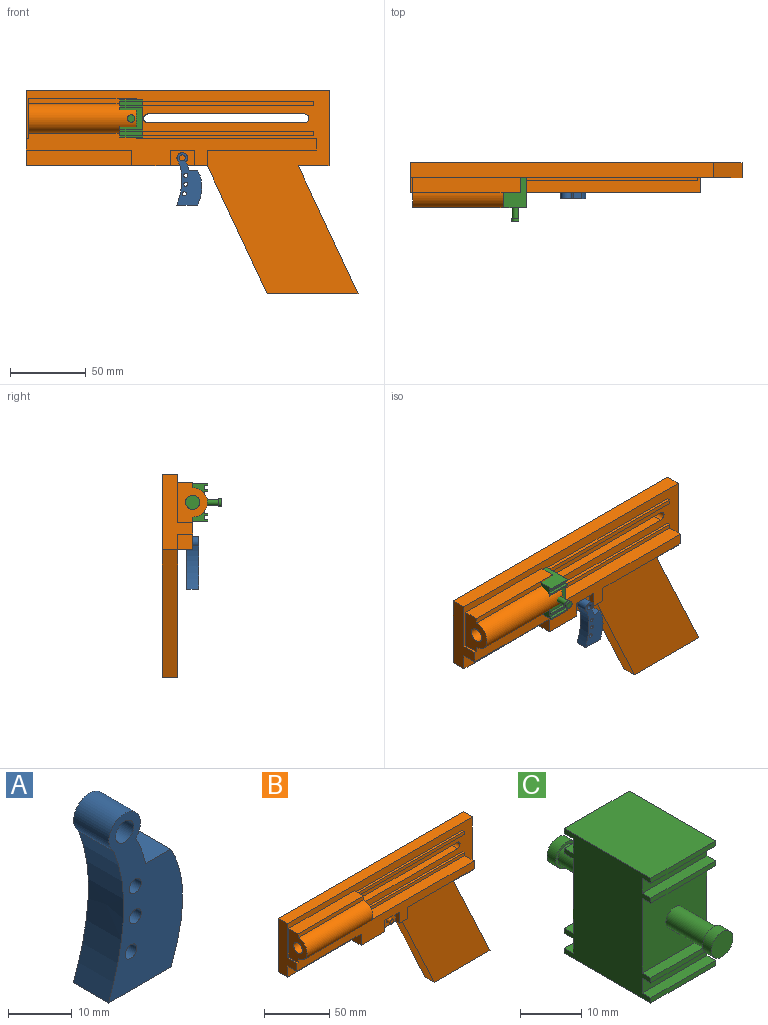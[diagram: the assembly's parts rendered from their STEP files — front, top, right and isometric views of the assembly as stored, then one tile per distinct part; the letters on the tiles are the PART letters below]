
ASSEMBLY  parts=3 mates=2
PART A: 13 faces, bbox 17.5x7.8x34.6 mm
  f0: plane 7.8x5.59mm, normal (0,0,1), area 43.6mm2, adj f1,f9,f11,f12
  f1: extruded ~7.8x5.93mm, area 49.6mm2, adj f0,f2,f11,f12
  f2: cylinder r=3.5mm len=7.8mm, axis (0,1,0), area 129.7mm2, adj f1,f3,f11,f12
  f3: extruded ~28.54x7.8mm, area 228.1mm2, adj f2,f4,f11,f12
  f4: plane 7.8x5.31mm, normal (-0.01,0,-1), area 41.4mm2, adj f3,f5,f11,f12
  f5: plane 8.48x7.8mm, normal (0,0,-1), area 66.1mm2, adj f4,f9,f11,f12
  f6: cylinder r=1.31mm len=7.8mm, axis (0,1,0), area 64.1mm2, adj f11,f12
  f7: cylinder r=1.31mm len=7.8mm, axis (0,1,0), area 64.1mm2, adj f11,f12
  f8: cylinder r=2mm len=7.8mm, axis (0,1,0), area 98mm2, adj f11,f12
  f9: extruded ~22.64x7.8mm, area 182.9mm2, adj f0,f5,f11,f12
  f10: cylinder r=1.31mm len=7.8mm, axis (0,1,0), area 64.1mm2, adj f11,f12
  f11: plane 34.6x17.46mm, normal (0,-1,0), area 333.6mm2, adj f0,f1,f2,f3,f4,f5,f6,f7
  f12: plane 34.6x17.46mm, normal (0,1,0), area 333.6mm2, adj f0,f1,f2,f3,f4,f5,f6,f7
PART B: 43 faces, bbox 219.1x29.7x134.5 mm
  f0: plane 119.24x10mm, normal (0,0,1), area 1192.4mm2, adj f3,f25,f28,f42
  f1: plane 69.74x10.47mm, normal (0,-1,0), area 730.2mm2, adj f8,f9,f27,f30
  f2: plane 72.17x10mm, normal (0,0,-1), area 721.7mm2, adj f3,f25,f28,f29
  f3: plane 219.13x134.46mm, normal (0,-1,0), area 9146.9mm2, adj f0,f2,f4,f5,f6,f7,f8,f10
  f4: plane 84.46x39.39mm, normal (0.91,0,0.42), area 931.9mm2, adj f3,f5,f11,f12
  f5: plane 20.26x10mm, normal (0,0,-1), area 202.6mm2, adj f3,f4,f6,f12
  f6: plane 50x10mm, normal (1,0,0), area 500mm2, adj f3,f5,f7,f12
  f7: plane 200x10mm, normal (0,0,1), area 2000mm2, adj f3,f6,f8,f12
  f8: plane 50x20mm, normal (-1,0,0), area 575.2mm2, adj f1,f3,f7,f9,f12,f26,f27,f28
  f9: plane 119.74x20mm, normal (0,0,-1), area 1633.9mm2, adj f1,f8,f10,f12,f28,f29,f30,f31
  f10: plane 84.46x39.39mm, normal (-0.91,0,-0.42), area 931.9mm2, adj f3,f9,f11,f12
  f11: plane 60x10mm, normal (0,0,-1), area 600mm2, adj f3,f4,f10,f12
  f12: plane 219.13x134.46mm, normal (0,1,0), area 14421.2mm2, adj f4,f5,f6,f7,f8,f9,f10,f11
  f13: plane 117.04x2mm, normal (0,0,-1), area 234.1mm2, adj f3,f14,f16,f42
  f14: plane 2.9x2mm, normal (1,0,0), area 5.8mm2, adj f3,f13,f15,f16
  f15: plane 117.04x2mm, normal (0,0,1), area 234.1mm2, adj f3,f14,f16,f42
  f16: plane 117.04x2.9mm, normal (0,-1,0), area 339.4mm2, adj f13,f14,f15,f42
  f17: plane 2.9x2mm, normal (1,0,0), area 5.8mm2, adj f3,f18,f19,f20
  f18: plane 117.04x2mm, normal (0,0,1), area 234.1mm2, adj f3,f17,f20,f42
  f19: plane 117.04x2mm, normal (0,0,-1), area 234.1mm2, adj f3,f17,f20,f42
  f20: plane 117.04x2.9mm, normal (0,-1,0), area 339.4mm2, adj f17,f18,f19,f42
  f21: cylinder r=3mm len=10mm, axis (0,1,0), area 94.2mm2, adj f3,f12,f22,f24
  f22: plane 103.05x10mm, normal (0,0,1), area 1030.5mm2, adj f3,f12,f21,f23
  f23: cylinder r=3mm len=10mm, axis (0,1,0), area 94.2mm2, adj f3,f12,f22,f24
  f24: plane 103.05x10mm, normal (0,0,-1), area 1030.5mm2, adj f3,f12,f21,f23
  f25: plane 10x7.52mm, normal (1,0,0), area 75.2mm2, adj f0,f2,f3,f28
  f26: plane 10x1.67mm, normal (0,0,1), area 16.7mm2, adj f3,f8,f28,f41
  f27: plane 69.74x10mm, normal (0,0,-1), area 697.4mm2, adj f1,f8,f28,f30
  f28: plane 191.91x21.64mm, normal (0,-1,0), area 2059.3mm2, adj f0,f2,f8,f9,f25,f26,f27,f29
  f29: plane 10.47x10mm, normal (1,0,0), area 104.7mm2, adj f2,f3,f9,f28
  f30: plane 10.47x10mm, normal (-1,0,0), area 104.7mm2, adj f1,f9,f27,f28
  f31: plane 10.47x4mm, normal (-1,0,0), area 41.9mm2, adj f9,f28,f32,f35
  f32: plane 15.88x4mm, normal (0,0,-1), area 63.5mm2, adj f28,f31,f34,f35
  f33: cylinder r=2mm len=4mm, axis (0,-1,0), area 50.3mm2, adj f35,f36
  f34: plane 10.47x4mm, normal (1,0,0), area 41.9mm2, adj f9,f28,f32,f35
  f35: plane 15.88x10.47mm, normal (0,-1,0), area 153.7mm2, adj f9,f31,f32,f33,f34
  f36: plane 4x4mm, normal (0,-1,0), area 12.6mm2, adj f33
  f37: cylinder r=9.72mm len=71mm, axis (1,0,0), area 2168.4mm2, adj f28,f38,f41,f42
  f38: plane 71x3.65mm, normal (0,-1,0), area 259.4mm2, adj f37,f39,f41,f42
  f39: plane 71x10mm, normal (0,0,1), area 710mm2, adj f3,f38,f41,f42
  f40: cylinder r=4.75mm len=71mm, axis (1,0,0), area 2119mm2, adj f41,f42
  f41: plane 26.75x19.72mm, normal (-1,0,0), area 345.1mm2, adj f3,f26,f28,f37,f38,f39,f40
  f42: plane 26.75x19.72mm, normal (1,0,0), area 333.5mm2, adj f0,f3,f13,f15,f16,f18,f19,f20
PART C: 38 faces, bbox 15x38x25 mm
  f0: plane 15x3mm, normal (0,1,0), area 45mm2, adj f7,f9,f34,f36
  f1: plane 15x15mm, normal (0,1,0), area 212.4mm2, adj f7,f9,f14,f31,f33
  f2: plane 15x3mm, normal (0,1,0), area 45mm2, adj f7,f9,f28,f30
  f3: plane 15x3mm, normal (0,-1,0), area 45mm2, adj f7,f9,f24,f26
  f4: plane 15x15mm, normal (0,-1,0), area 212.4mm2, adj f7,f9,f10,f21,f23
  f5: plane 15x3mm, normal (0,-1,0), area 45mm2, adj f7,f9,f18,f20
  f6: plane 20x15mm, normal (0,0,1), area 300mm2, adj f7,f9,f19,f29
  f7: plane 25x20mm, normal (-1,0,0), area 416mm2, adj f0,f1,f2,f3,f4,f5,f6,f8
  f8: plane 20x15mm, normal (0,0,-1), area 300mm2, adj f7,f9,f27,f37
  f9: plane 25x20mm, normal (1,0,0), area 416mm2, adj f0,f1,f2,f3,f4,f5,f6,f8
  f10: cylinder r=2mm len=9mm, axis (0,1,0), area 113.1mm2, adj f4,f13
  f11: cylinder r=2.5mm len=5mm, axis (0,1,0), area 31.4mm2, adj f12,f13
  f12: plane 5x5mm, normal (0,-1,0), area 19.6mm2, adj f11
  f13: plane 5x5mm, normal (0,1,0), area 7.1mm2, adj f10,f11
  f14: cylinder r=2mm len=9mm, axis (0,-1,0), area 113.1mm2, adj f1,f17
  f15: cylinder r=2.5mm len=5mm, axis (0,-1,0), area 31.4mm2, adj f16,f17
  f16: plane 5x5mm, normal (0,1,0), area 19.6mm2, adj f15
  f17: plane 5x5mm, normal (0,-1,0), area 7.1mm2, adj f14,f15
  f18: plane 15x2mm, normal (0,0,-1), area 30mm2, adj f5,f7,f9,f19
  f19: plane 15x1mm, normal (0,-1,0), area 15mm2, adj f6,f7,f9,f18
  f20: plane 15x2mm, normal (0,0,1), area 30mm2, adj f5,f7,f9,f22
  f21: plane 15x2mm, normal (0,0,-1), area 30mm2, adj f4,f7,f9,f22
  f22: plane 15x1mm, normal (0,-1,0), area 15mm2, adj f7,f9,f20,f21
  f23: plane 15x2mm, normal (0,0,1), area 30mm2, adj f4,f7,f9,f25
  f24: plane 15x2mm, normal (0,0,-1), area 30mm2, adj f3,f7,f9,f25
  f25: plane 15x1mm, normal (0,-1,0), area 15mm2, adj f7,f9,f23,f24
  f26: plane 15x2mm, normal (0,0,1), area 30mm2, adj f3,f7,f9,f27
  f27: plane 15x1mm, normal (0,-1,0), area 15mm2, adj f7,f8,f9,f26
  f28: plane 15x2mm, normal (0,0,-1), area 30mm2, adj f2,f7,f9,f29
  f29: plane 15x1mm, normal (0,1,0), area 15mm2, adj f6,f7,f9,f28
  f30: plane 15x2mm, normal (0,0,1), area 30mm2, adj f2,f7,f9,f32
  f31: plane 15x2mm, normal (0,0,-1), area 30mm2, adj f1,f7,f9,f32
  f32: plane 15x1mm, normal (0,1,0), area 15mm2, adj f7,f9,f30,f31
  f33: plane 15x2mm, normal (0,0,1), area 30mm2, adj f1,f7,f9,f35
  f34: plane 15x2mm, normal (0,0,-1), area 30mm2, adj f0,f7,f9,f35
  f35: plane 15x1mm, normal (0,1,0), area 15mm2, adj f7,f9,f33,f34
  f36: plane 15x2mm, normal (0,0,1), area 30mm2, adj f0,f7,f9,f37
  f37: plane 15x1mm, normal (0,1,0), area 15mm2, adj f7,f8,f9,f36
PLACE A t=(-31.75,-18.04,-1.95)mm
PLACE B t=(-31.75,-18.04,-1.95)mm
PLACE C t=(-132.99,-18.04,-2.07)mm
MATE revolute A.f2 <-> B.f33  axis (0,1,0) through (-74.07,-34.04,-16.07)mm
MATE pin_slot C.f2 <-> B.f16  axis (0,1,0) through (-100.28,-30.04,20)mm
